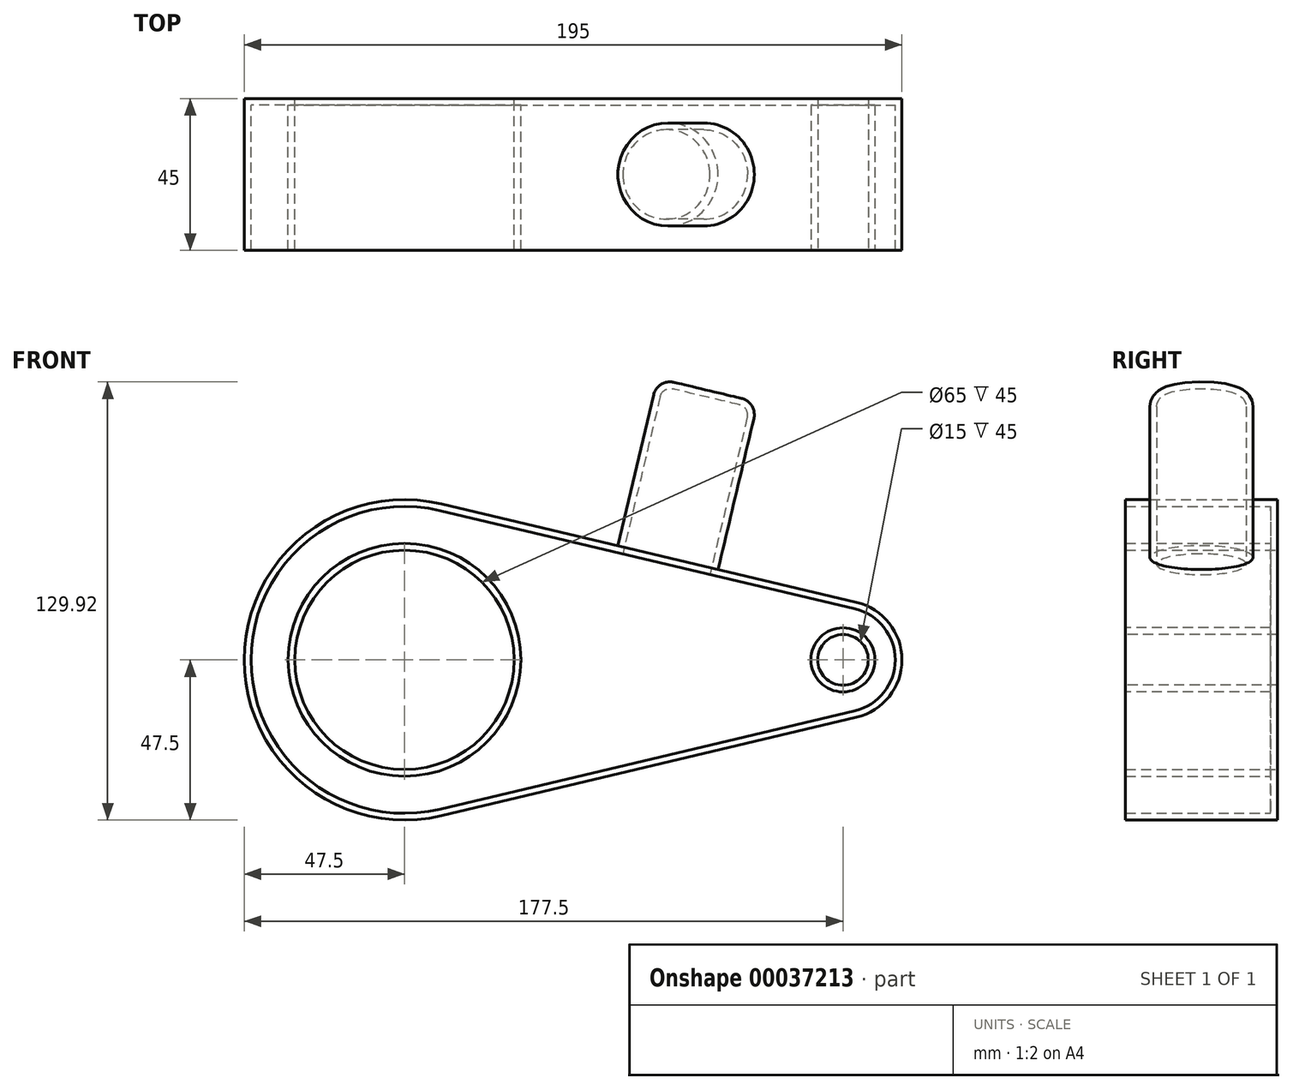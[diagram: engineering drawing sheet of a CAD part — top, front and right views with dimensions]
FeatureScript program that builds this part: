
annotation { "Feature Type Name" : "Feature", "Feature Type Description" : "" }
export const myFeature = defineFeature(function(context is Context, id is Id, definition is map)
    precondition{}
    {
        {
            var Q0;
            Q0=qCreatedBy(makeId("Front.planeOp"),FACE);
            var sketch = newSketch(context, id + "F0", { "sketchPlane" : qUnion([Q0])});
            skCircle(sketch, "E0", {"center": v(0, 0) * mm, "radius": 47.5 * mm});
            skCircle(sketch, "E1", {"center": v(130, 0) * mm, "radius": 17.5 * mm});
            skLineSegment(sketch, "E2", {"start": v(10.96, 46.22) * mm, "end": v(134.04, 17.03) * mm});
            skLineSegment(sketch, "E3", {"start": v(10.96, -46.22) * mm, "end": v(134.04, -17.03) * mm});
            skCircle(sketch, "E4", {"center": v(0, 0) * mm, "radius": 32.5 * mm});
            skSolve(sketch);
        }
        {
            var Q0;
            Q0 = qSketchRegion(id + "F0", true);
            extrude(context, id + "F1", {"entities" : qUnion([Q0]), "depth" : 45 * mm});
        }
        {
            var Q0;
            Q0=makeQuery(id+"F1.opExtrude","SWEPT_FACE",FACE,{"disambiguationData":[OSD([sQuery(id+"F0.wireOp",EDGE,"E2")])]});
            var sketch = newSketch(context, id + "F2", { "sketchPlane" : qUnion([Q0])});
            skCircle(sketch, "E5", {"center": v(69.01, -22.5) * mm, "radius": 15.27 * mm});
            skPoint(sketch, "E5.centerSnap0", {"position": v(126.5, -22.5) * mm});
            skSolve(sketch);
        }
        {
            var Q0;
            Q0 = qSketchRegion(id + "F2", true);
            extrude(context, id + "F3", {"entities" : qUnion([Q0]), "operationType" : NewBodyOperationType.ADD, "depth" : 51 * mm});
        }
        {
            var Q0;
            Q0=makeQuery(id+"F3.opExtrude","CAP_EDGE",EDGE,{"disambiguationData":[OSD([sQuery(id+"F2.wireOp",EDGE,"E5")])],"isStart":false});
            var Q1;
            Q1=makeQuery(id+"F3.opExtrude","CAP_EDGE",EDGE,{"disambiguationData":[OSD([sQuery(id+"F2.wireOp",EDGE,"E5")])],"isStart":true});
            fillet(context, id + "F4", {"entities" : qUnion([Q0, Q1]), "radius" : 5 * mm, "tangentPropagation" : true, "allowEdgeOverflow" : false});
        }
        {
            var Q0;
            Q0=makeQuery(id+"F1.opExtrude","CAP_FACE",FACE,{"disambiguationData":[OSD([sQuery(id+"F0.wireOp",EDGE,"E0"),sQuery(id+"F0.wireOp",EDGE,"E1"),sQuery(id+"F0.wireOp",EDGE,"E2"),sQuery(id+"F0.wireOp",EDGE,"E3"),sQuery(id+"F0.wireOp",EDGE,"E4")])],"isStart":false});
            var sketch = newSketch(context, id + "F5", { "sketchPlane" : qUnion([Q0])});
            skCircle(sketch, "E6", {"center": v(130, 0) * mm, "radius": 7.5 * mm});
            skSolve(sketch);
        }
        {
            var Q0;
            Q0 = qSketchRegion(id + "F5", true);
            extrude(context, id + "F6", {"entities" : qUnion([Q0]), "operationType" : NewBodyOperationType.REMOVE, "endBound" : BoundingType.THROUGH_ALL, "oppositeDirection" : true, "depth" : 25 * mm});
        }
        {
            var Q0;
            Q0=makeQuery(id+"F1.opExtrude","CAP_FACE",FACE,{"disambiguationData":[OSD([sQuery(id+"F0.wireOp",EDGE,"E0"),sQuery(id+"F0.wireOp",EDGE,"E1"),sQuery(id+"F0.wireOp",EDGE,"E2"),sQuery(id+"F0.wireOp",EDGE,"E3"),sQuery(id+"F0.wireOp",EDGE,"E4")])],"isStart":false});
            shell(context, id + "F7", {"entities" : qUnion([Q0]), "thickness" : 2 * mm});
        }
    });
